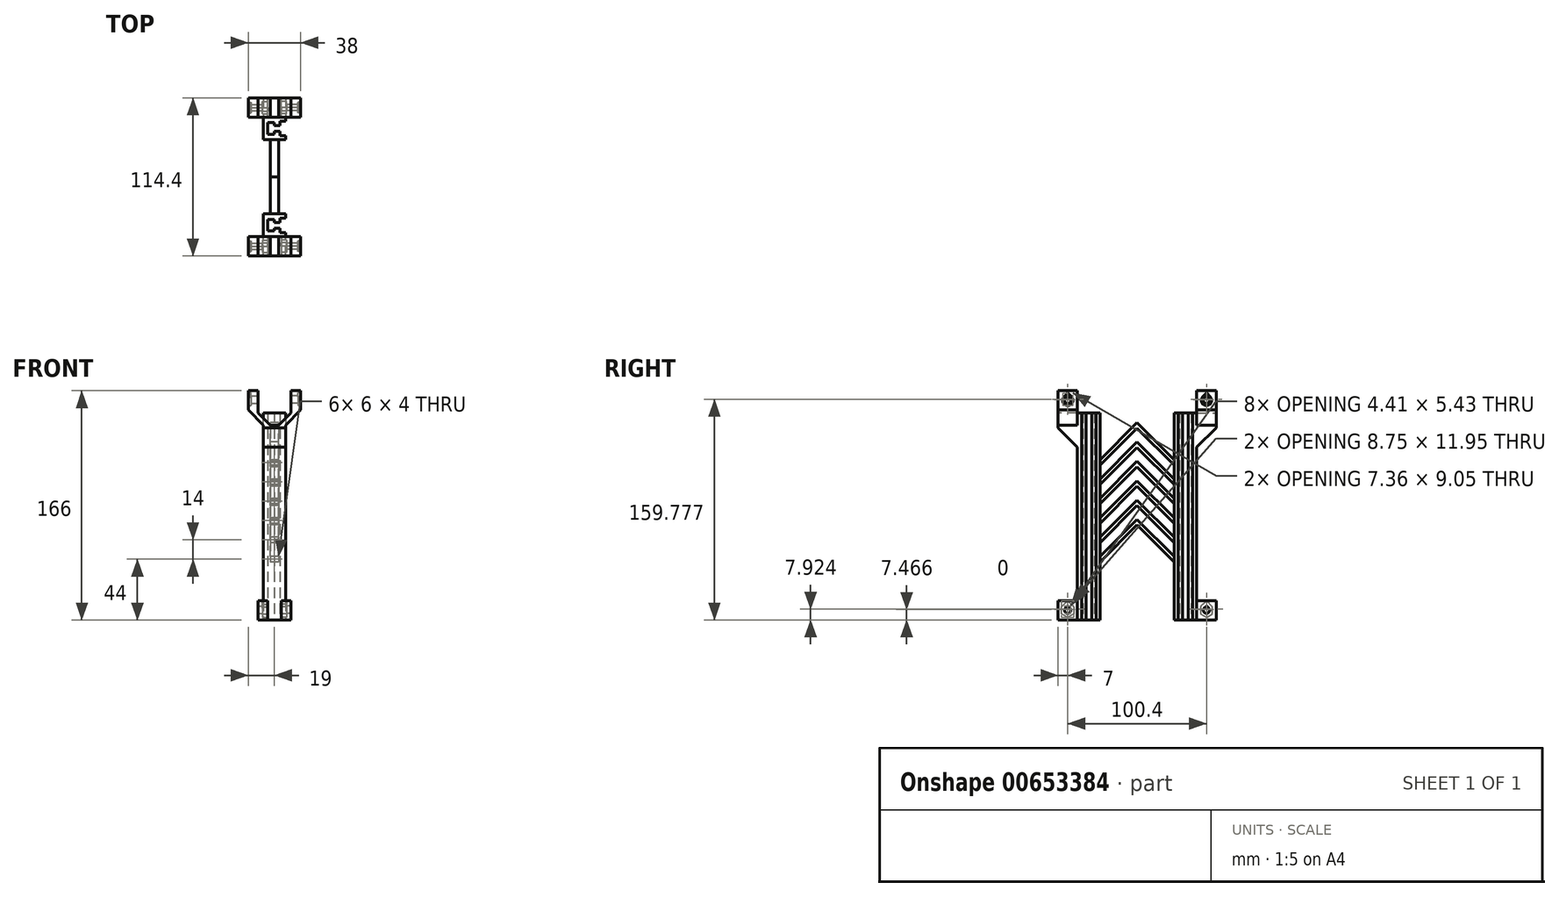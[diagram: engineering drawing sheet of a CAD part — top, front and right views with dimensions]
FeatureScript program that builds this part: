
annotation { "Feature Type Name" : "Feature", "Feature Type Description" : "" }
export const myFeature = defineFeature(function(context is Context, id is Id, definition is map)
    precondition{}
    {
        {
            var Q0;
            Q0=qCreatedBy(makeId("Top.planeOp"),FACE);
            var sketch = newSketch(context, id + "F0", { "sketchPlane" : qUnion([Q0])});
            skLineSegment(sketch, "E0", {"start": v(0, 0) * mm, "end": v(5, 0) * mm});
            skLineSegment(sketch, "E1", {"start": v(5, 0) * mm, "end": v(5, -2.1) * mm});
            skLineSegment(sketch, "E2", {"start": v(5, -2.1) * mm, "end": v(9, -2.1) * mm});
            skLineSegment(sketch, "E3", {"start": v(9, -2.1) * mm, "end": v(9, 1) * mm});
            skLineSegment(sketch, "E4", {"start": v(9, 1) * mm, "end": v(13, 1) * mm});
            skLineSegment(sketch, "E5", {"start": v(13, 1) * mm, "end": v(13, 4) * mm});
            skLineSegment(sketch, "E6", {"start": v(13, 4) * mm, "end": v(-3, 4) * mm});
            skLineSegment(sketch, "E7", {"start": v(-3, 4) * mm, "end": v(-3, -12.4) * mm});
            skLineSegment(sketch, "E8", {"start": v(-3, -12.4) * mm, "end": v(13, -12.4) * mm});
            skLineSegment(sketch, "E9", {"start": v(13, -12.4) * mm, "end": v(13, -9.4) * mm});
            skLineSegment(sketch, "E10", {"start": v(13, -9.4) * mm, "end": v(9, -9.4) * mm});
            skLineSegment(sketch, "E11", {"start": v(9, -9.4) * mm, "end": v(9, -6.3) * mm});
            skLineSegment(sketch, "E12", {"start": v(9, -6.3) * mm, "end": v(5, -6.3) * mm});
            skLineSegment(sketch, "E13", {"start": v(5, -6.3) * mm, "end": v(5, -8.4) * mm});
            skLineSegment(sketch, "E14", {"start": v(5, -8.4) * mm, "end": v(0, -8.4) * mm});
            skLineSegment(sketch, "E15", {"start": v(0, -8.4) * mm, "end": v(0, 0) * mm});
            skLineSegment(sketch, "E16", {"start": v(0, 0) * mm, "end": v(-3, 0) * mm});
            skLineSegment(sketch, "E17", {"start": v(0, -8.4) * mm, "end": v(-3, -8.4) * mm});
            skLineSegment(sketch, "E18", {"start": v(13, -9.4) * mm, "end": v(13, 1) * mm});
            skLineSegment(sketch, "E19", {"start": v(13, -12.4) * mm, "end": v(9.8, -12.4) * mm});
            skLineSegment(sketch, "E20", {"start": v(13, -12.4) * mm, "end": v(5, -12.4) * mm});
            skSolve(sketch);
        }
        {
            var Q0;
            Q0=makeQuery(id+"F0.imprint","IMPRINT",FACE,{"disambiguationData":[TD([[makeQuery(id+"F0.imprint","IMPRINT",EDGE,{"derivedFrom":sQuery(id+"F0.wireOp",EDGE,"E0")}),1.0]])]});
            var Q1;
            {var subQ0=sQuery(id+"F0.wireOp",EDGE,"E8");Q1=makeQuery(id+"F0.imprint","IMPRINT",FACE,{"disambiguationData":[TD([[makeQuery(id+"F0.imprint","IMPRINT",EDGE,{"derivedFrom":subQ0}),1.0]])]});}
            var Q2;
            Q2=makeQuery(id+"F0.imprint","IMPRINT",FACE,{"disambiguationData":[TD([[makeQuery(id+"F0.imprint","IMPRINT",EDGE,{"derivedFrom":sQuery(id+"F0.wireOp",EDGE,"E15")}),1.0]])]});
            extrude(context, id + "F1", {"entities" : qUnion([Q0, Q1, Q2]), "depth" : 150 * mm, "offsetDistance" : 25 * mm});
        }
        {
            var Q0;
            Q0=sQuery(id+"F0.wireOp",EDGE,"E8");
            var Q1;
            Q1=sQuery(id+"F0.wireOp",VERTEX,"E19.end");
            cPlane(context, id + "F2", {"entities" : qUnion([Q0, Q1]), "cplaneType" : CPlaneType.LINE_POINT, "offset" : 25 * mm, "width" : 150 * mm, "height" : 150 * mm});
        }
        {
            var Q0;
            Q0=qCreatedBy(id+"F2.planeOp",FACE);
            var sketch = newSketch(context, id + "F3", { "sketchPlane" : qUnion([Q0])});
            skPoint(sketch, "E21.0", {"position": v(-12.4, 0) * mm});
            skLineSegment(sketch, "E22.bottom", {"start": v(-12.4, 0) * mm, "end": v(-26.4, 0) * mm});
            skLineSegment(sketch, "E22.top", {"start": v(-12.4, 14) * mm, "end": v(-26.4, 14) * mm});
            skLineSegment(sketch, "E22.left", {"start": v(-12.4, 0) * mm, "end": v(-12.4, 14) * mm});
            skLineSegment(sketch, "E22.right", {"start": v(-26.4, 0) * mm, "end": v(-26.4, 14) * mm});
            skLineSegment(sketch, "E23", {"start": v(-19.4, 0) * mm, "end": v(-19.4, 7) * mm});
            skCircle(sketch, "E24", {"center": v(-19.4, 7) * mm, "radius": 5.05 * mm});
            skCircle(sketch, "E25.cCircle", {"center": v(-19.4, 7) * mm, "radius": 5.05 * mm, "construction": true});
            skLineSegment(sketch, "E25.0", {"start": v(-19.4, 12.05) * mm, "end": v(-15.03, 9.53) * mm});
            skLineSegment(sketch, "E25.1", {"start": v(-15.03, 9.53) * mm, "end": v(-15.03, 4.48) * mm});
            skLineSegment(sketch, "E25.2", {"start": v(-15.03, 4.48) * mm, "end": v(-19.4, 1.95) * mm});
            skLineSegment(sketch, "E25.3", {"start": v(-19.4, 1.95) * mm, "end": v(-23.77, 4.47) * mm});
            skLineSegment(sketch, "E25.4", {"start": v(-23.77, 4.47) * mm, "end": v(-23.77, 9.52) * mm});
            skLineSegment(sketch, "E25.5", {"start": v(-23.77, 9.52) * mm, "end": v(-19.4, 12.05) * mm});
            skLineSegment(sketch, "E26", {"start": v(-19.4, 7) * mm, "end": v(-24.45, 7) * mm});
            skLineSegment(sketch, "E27", {"start": v(-24.45, 7) * mm, "end": v(-19.4, 12.05) * mm});
            skLineSegment(sketch, "E28", {"start": v(-23.77, 9.52) * mm, "end": v(-19.4, 13.9) * mm});
            skLineSegment(sketch, "E29", {"start": v(-19.4, 13.9) * mm, "end": v(-15.03, 9.53) * mm});
            skLineSegment(sketch, "E30", {"start": v(-15.03, 9.53) * mm, "end": v(-16.88, 11.37) * mm});
            skSolve(sketch);
        }
        {
            var Q0;
            Q0=makeQuery(id+"F3.imprint","IMPRINT",FACE,{"disambiguationData":[TD([[makeQuery(id+"F3.imprint","IMPRINT",EDGE,{"derivedFrom":sQuery(id+"F3.wireOp",EDGE,"E22.top")}),1.0]])]});
            var Q1;
            {var subQ0=sQuery(id+"F3.wireOp",EDGE,"E25.1");Q1=makeQuery(id+"F3.imprint","IMPRINT",FACE,{"disambiguationData":[TD([[makeQuery(id+"F3.imprint","IMPRINT",EDGE,{"derivedFrom":subQ0}),1.0]])]});}
            var Q2;
            {var subQ0=sQuery(id+"F3.wireOp",EDGE,"E25.2");Q2=makeQuery(id+"F3.imprint","IMPRINT",FACE,{"disambiguationData":[TD([[makeQuery(id+"F3.imprint","IMPRINT",EDGE,{"derivedFrom":subQ0}),1.0]])]});}
            var Q3;
            {var subQ0=sQuery(id+"F3.wireOp",EDGE,"E25.3");Q3=makeQuery(id+"F3.imprint","IMPRINT",FACE,{"disambiguationData":[TD([[makeQuery(id+"F3.imprint","IMPRINT",EDGE,{"derivedFrom":subQ0}),1.0]])]});}
            var Q4;
            {var subQ0=sQuery(id+"F3.wireOp",EDGE,"E25.4");Q4=makeQuery(id+"F3.imprint","IMPRINT",FACE,{"disambiguationData":[TD([[makeQuery(id+"F3.imprint","IMPRINT",EDGE,{"derivedFrom":subQ0}),1.0]])]});}
            var Q5;
            {var subQ0=sQuery(id+"F3.wireOp",EDGE,"E28");var subQ1=sQuery(id+"F3.wireOp",EDGE,"E24");var subQ3=makeQuery(id+"F3.imprint","INTERSECT",VERTEX,{"derivedFrom":[subQ1,subQ0]});Q5=makeQuery(id+"F3.imprint","IMPRINT",FACE,{"disambiguationData":[TD([[makeQuery(id+"F3.imprint","IMPRINT",EDGE,{"disambiguationData":[TD([[subQ3,-1.0]])],"derivedFrom":subQ1}),1.0]])]});}
            var Q6;
            {var subQ0=sQuery(id+"F3.wireOp",EDGE,"E30");Q6=makeQuery(id+"F3.imprint","IMPRINT",FACE,{"disambiguationData":[TD([[makeQuery(id+"F3.imprint","IMPRINT",EDGE,{"derivedFrom":subQ0}),-1.0]])]});}
            extrude(context, id + "F4", {"entities" : qUnion([Q0, Q1, Q2, Q3, Q4, Q5, Q6]), "depth" : 4 * mm, "offsetDistance" : 25 * mm});
        }
        {
            var Q0;
            Q0=makeQuery(id+"F4.opExtrude","CAP_FACE",FACE,{"disambiguationData":[OSD([sQuery(id+"F3.wireOp",EDGE,"E22.bottom"),sQuery(id+"F3.wireOp",EDGE,"E22.top"),sQuery(id+"F3.wireOp",EDGE,"E22.left"),sQuery(id+"F3.wireOp",EDGE,"E22.right"),sQuery(id+"F3.wireOp",EDGE,"E25.0"),sQuery(id+"F3.wireOp",EDGE,"E25.1"),sQuery(id+"F3.wireOp",EDGE,"E25.2"),sQuery(id+"F3.wireOp",EDGE,"E25.3"),sQuery(id+"F3.wireOp",EDGE,"E25.4"),sQuery(id+"F3.wireOp",EDGE,"E25.5")])],"isStart":false});
            var sketch = newSketch(context, id + "F5", { "sketchPlane" : qUnion([Q0])});
            skPoint(sketch, "E31.0", {"position": v(-19.4, 7) * mm});
            skLineSegment(sketch, "E32.bottom", {"start": v(-12.4, 0) * mm, "end": v(-26.4, 0) * mm});
            skLineSegment(sketch, "E32.top", {"start": v(-12.4, 14) * mm, "end": v(-26.4, 14) * mm});
            skLineSegment(sketch, "E32.left", {"start": v(-12.4, 0) * mm, "end": v(-12.4, 14) * mm});
            skLineSegment(sketch, "E32.right", {"start": v(-26.4, 0) * mm, "end": v(-26.4, 14) * mm});
            skCircle(sketch, "E33", {"center": v(-19.4, 7) * mm, "radius": 2.25 * mm});
            skLineSegment(sketch, "E34", {"start": v(-17.15, 7) * mm, "end": v(-19.4, 9.25) * mm});
            skLineSegment(sketch, "E35", {"start": v(-19.4, 7) * mm, "end": v(-17.8, 8.6) * mm});
            skLineSegment(sketch, "E36", {"start": v(-17.8, 8.6) * mm, "end": v(-19.4, 10.18) * mm});
            skLineSegment(sketch, "E37", {"start": v(-19.4, 10.18) * mm, "end": v(-21, 8.6) * mm});
            skSolve(sketch);
        }
        {
            var Q0;
            Q0=makeQuery(id+"F5.imprint","IMPRINT",FACE,{"disambiguationData":[TD([[makeQuery(id+"F5.imprint","IMPRINT",EDGE,{"derivedFrom":sQuery(id+"F5.wireOp",EDGE,"E32.bottom")}),-1.0]])]});
            var Q1;
            {var subQ0=sQuery(id+"F5.wireOp",EDGE,"E36");Q1=makeQuery(id+"F5.imprint","IMPRINT",FACE,{"disambiguationData":[TD([[makeQuery(id+"F5.imprint","IMPRINT",EDGE,{"derivedFrom":subQ0}),-1.0]])]});}
            extrude(context, id + "F6", {"entities" : qUnion([Q0, Q1]), "operationType" : NewBodyOperationType.ADD, "depth" : 3 * mm, "offsetDistance" : 25 * mm});
        }
        {
            var Q0;
            Q0=sQuery(id+"F0.wireOp",EDGE,"E8");
            var Q1;
            Q1=sQuery(id+"F0.wireOp",VERTEX,"E20.end");
            cPlane(context, id + "F7", {"entities" : qUnion([Q0, Q1]), "cplaneType" : CPlaneType.LINE_POINT, "offset" : 25 * mm, "width" : 150 * mm, "height" : 150 * mm});
        }
        {
            var Q0;
            Q0=makeQuery(id+"F4.opExtrude","SWEPT_BODY",BODY,{"disambiguationData":[OSD([sQuery(id+"F3.wireOp",EDGE,"E22.bottom"),sQuery(id+"F3.wireOp",EDGE,"E22.top"),sQuery(id+"F3.wireOp",EDGE,"E22.left"),sQuery(id+"F3.wireOp",EDGE,"E22.right"),sQuery(id+"F3.wireOp",EDGE,"E25.0"),sQuery(id+"F3.wireOp",EDGE,"E25.1"),sQuery(id+"F3.wireOp",EDGE,"E25.2"),sQuery(id+"F3.wireOp",EDGE,"E25.3"),sQuery(id+"F3.wireOp",EDGE,"E25.4"),sQuery(id+"F3.wireOp",EDGE,"E25.5")])]});
            var Q1;
            Q1=makeQuery(id+"F6.opExtrude","SWEPT_BODY",BODY,{"disambiguationData":[OSD([sQuery(id+"F5.wireOp",EDGE,"E32.bottom"),sQuery(id+"F5.wireOp",EDGE,"E32.top"),sQuery(id+"F5.wireOp",EDGE,"E32.left"),sQuery(id+"F5.wireOp",EDGE,"E32.right"),sQuery(id+"F5.wireOp",EDGE,"E33")])]});
            var Q2;
            Q2=qCreatedBy(id+"F7.planeOp",FACE);
            mirror(context, id + "F8", {"operationType" : NewBodyOperationType.ADD, "entities" : qUnion([Q0, Q1]), "mirrorPlane" : qUnion([Q2])});
        }
        {
            var Q0;
            Q0=makeQuery(id+"F1.opExtrude","SWEPT_FACE",FACE,{"disambiguationData":[OSD([sQuery(id+"F0.wireOp",EDGE,"E7")])]});
            var sketch = newSketch(context, id + "F9", { "sketchPlane" : qUnion([Q0])});
            skPoint(sketch, "E38.0", {"position": v(12.4, 150) * mm});
            skLineSegment(sketch, "E39", {"start": v(12.4, 150) * mm, "end": v(12.4, 125) * mm});
            skLineSegment(sketch, "E40", {"start": v(12.4, 125) * mm, "end": v(26.4, 125) * mm});
            skLineSegment(sketch, "E41", {"start": v(26.4, 125) * mm, "end": v(26.4, 139) * mm});
            skLineSegment(sketch, "E42", {"start": v(26.4, 139) * mm, "end": v(12.4, 125) * mm});
            skLineSegment(sketch, "E43", {"start": v(26.4, 139) * mm, "end": v(26.4, 141) * mm});
            skLineSegment(sketch, "E44", {"start": v(26.4, 141) * mm, "end": v(12.4, 141) * mm});
            skSolve(sketch);
        }
        {
            var Q0;
            {var subQ0=sQuery(id+"F9.wireOp",EDGE,"E42");Q0=makeQuery(id+"F9.imprint","IMPRINT",FACE,{"disambiguationData":[TD([[makeQuery(id+"F9.imprint","IMPRINT",EDGE,{"derivedFrom":subQ0}),-1.0]])]});}
            extrude(context, id + "F10", {"entities" : qUnion([Q0]), "oppositeDirection" : true, "depth" : 16 * mm, "offsetDistance" : 25 * mm});
        }
        {
            var Q0;
            Q0=makeQuery(id+"F10.opExtrude","SWEPT_FACE",FACE,{"disambiguationData":[OSD([sQuery(id+"F9.wireOp",EDGE,"E43")])]});
            var sketch = newSketch(context, id + "F11", { "sketchPlane" : qUnion([Q0])});
            skPoint(sketch, "E45.0", {"position": v(13, 141) * mm});
            skPoint(sketch, "E46.0", {"position": v(-3, 141) * mm});
            skLineSegment(sketch, "E47", {"start": v(13, 141) * mm, "end": v(24, 141) * mm});
            skLineSegment(sketch, "E48", {"start": v(24, 141) * mm, "end": v(24, 152) * mm});
            skLineSegment(sketch, "E49", {"start": v(24, 152) * mm, "end": v(13, 141) * mm});
            skLineSegment(sketch, "E50", {"start": v(24, 152) * mm, "end": v(17, 152) * mm});
            skLineSegment(sketch, "E51", {"start": v(17, 152) * mm, "end": v(17, 150) * mm});
            skLineSegment(sketch, "E52", {"start": v(17, 150) * mm, "end": v(8, 141) * mm});
            skLineSegment(sketch, "E53", {"start": v(5, 141) * mm, "end": v(5, 151) * mm});
            skLineSegment(sketch, "E54.MirrorCS", {"start": v(-7, 150) * mm, "end": v(2, 141) * mm});
            skLineSegment(sketch, "E55.MirrorCS", {"start": v(-7, 152) * mm, "end": v(-7, 150) * mm});
            skLineSegment(sketch, "E56.MirrorCS", {"start": v(-14, 152) * mm, "end": v(-7, 152) * mm});
            skLineSegment(sketch, "E57.MirrorCS", {"start": v(-3, 141) * mm, "end": v(-14, 141) * mm});
            skLineSegment(sketch, "E58.MirrorCS", {"start": v(-14, 152) * mm, "end": v(-3, 141) * mm});
            skLineSegment(sketch, "E59.MirrorCS", {"start": v(-14, 141) * mm, "end": v(-14, 152) * mm});
            skSolve(sketch);
        }
        {
            var Q0;
            {var subQ1=sQuery(id+"F11.wireOp",EDGE,"E49");Q0=makeQuery(id+"F11.imprint","IMPRINT",FACE,{"disambiguationData":[TD([[makeQuery(id+"F11.imprint","IMPRINT",EDGE,{"derivedFrom":subQ1}),-1.0]])]});}
            var Q1;
            {var subQ1=sQuery(id+"F11.wireOp",EDGE,"E54.MirrorCS");Q1=makeQuery(id+"F11.imprint","IMPRINT",FACE,{"disambiguationData":[TD([[makeQuery(id+"F11.imprint","IMPRINT",EDGE,{"derivedFrom":subQ1}),-1.0]])]});}
            extrude(context, id + "F12", {"entities" : qUnion([Q0, Q1]), "oppositeDirection" : true, "depth" : 14 * mm, "offsetDistance" : 25 * mm});
        }
        {
            var Q0;
            Q0=makeQuery(id+"F12.opExtrude","SWEPT_FACE",FACE,{"disambiguationData":[OSD([sQuery(id+"F11.wireOp",EDGE,"E55.MirrorCS")])]});
            var sketch = newSketch(context, id + "F13", { "sketchPlane" : qUnion([Q0])});
            skPoint(sketch, "E60.0", {"position": v(-19.4, 152) * mm});
            skLineSegment(sketch, "E61", {"start": v(-19.4, 152) * mm, "end": v(-19.4, 159) * mm});
            skLineSegment(sketch, "E62.bottom", {"start": v(-12.4, 152) * mm, "end": v(-26.4, 152) * mm});
            skLineSegment(sketch, "E62.top", {"start": v(-12.4, 166) * mm, "end": v(-26.4, 166) * mm});
            skLineSegment(sketch, "E62.left", {"start": v(-12.4, 152) * mm, "end": v(-12.4, 166) * mm});
            skLineSegment(sketch, "E62.right", {"start": v(-26.4, 152) * mm, "end": v(-26.4, 166) * mm});
            skPoint(sketch, "E62.middle", {"position": v(-19.4, 159) * mm});
            skCircle(sketch, "E63", {"center": v(-19.4, 159) * mm, "radius": 2.25 * mm});
            skLineSegment(sketch, "E64", {"start": v(-17.15, 159) * mm, "end": v(-19.4, 161.25) * mm});
            skLineSegment(sketch, "E65", {"start": v(-19.4, 159) * mm, "end": v(-17.8, 160.6) * mm});
            skLineSegment(sketch, "E66", {"start": v(-17.8, 160.6) * mm, "end": v(-19.4, 162.18) * mm});
            skLineSegment(sketch, "E67", {"start": v(-19.4, 162.18) * mm, "end": v(-21, 160.6) * mm});
            skSolve(sketch);
        }
        {
            var Q0;
            Q0=makeQuery(id+"F13.imprint","IMPRINT",FACE,{"disambiguationData":[TD([[makeQuery(id+"F13.imprint","IMPRINT",EDGE,{"derivedFrom":sQuery(id+"F13.wireOp",EDGE,"E62.top")}),1.0]])]});
            extrude(context, id + "F14", {"entities" : qUnion([Q0]), "oppositeDirection" : true, "depth" : 5 * mm, "offsetDistance" : 25 * mm});
        }
        {
            var Q0;
            Q0=makeQuery(id+"F14.opExtrude","CAP_FACE",FACE,{"disambiguationData":[OSD([sQuery(id+"F13.wireOp",EDGE,"E62.bottom"),sQuery(id+"F13.wireOp",EDGE,"E62.top"),sQuery(id+"F13.wireOp",EDGE,"E62.left"),sQuery(id+"F13.wireOp",EDGE,"E62.right"),sQuery(id+"F13.wireOp",EDGE,"E63")])],"isStart":false});
            var sketch = newSketch(context, id + "F15", { "sketchPlane" : qUnion([Q0])});
            skPoint(sketch, "E68.0", {"position": v(19.4, 159) * mm});
            skLineSegment(sketch, "E69.bottom", {"start": v(26.4, 166) * mm, "end": v(12.4, 166) * mm});
            skLineSegment(sketch, "E69.top", {"start": v(26.4, 152) * mm, "end": v(12.4, 152) * mm});
            skLineSegment(sketch, "E69.left", {"start": v(26.4, 166) * mm, "end": v(26.4, 152) * mm});
            skLineSegment(sketch, "E69.right", {"start": v(12.4, 166) * mm, "end": v(12.4, 152) * mm});
            skCircle(sketch, "E70", {"center": v(19.4, 159) * mm, "radius": 3.75 * mm});
            skLineSegment(sketch, "E71", {"start": v(23.15, 159) * mm, "end": v(19.4, 162.75) * mm});
            skLineSegment(sketch, "E72", {"start": v(19.4, 159) * mm, "end": v(22.05, 161.65) * mm});
            skLineSegment(sketch, "E73", {"start": v(22.05, 161.65) * mm, "end": v(19.4, 164.3) * mm});
            skLineSegment(sketch, "E74", {"start": v(19.4, 164.3) * mm, "end": v(16.75, 161.65) * mm});
            skSolve(sketch);
        }
        {
            var Q0;
            Q0=makeQuery(id+"F15.imprint","IMPRINT",FACE,{"disambiguationData":[TD([[makeQuery(id+"F15.imprint","IMPRINT",EDGE,{"derivedFrom":sQuery(id+"F15.wireOp",EDGE,"E69.bottom")}),-1.0]])]});
            extrude(context, id + "F16", {"entities" : qUnion([Q0]), "depth" : 2 * mm, "offsetDistance" : 25 * mm});
        }
        {
            var Q0;
            Q0=makeQuery(id+"F14.opExtrude","SWEPT_BODY",BODY,{"disambiguationData":[OSD([sQuery(id+"F13.wireOp",EDGE,"E62.bottom"),sQuery(id+"F13.wireOp",EDGE,"E62.top"),sQuery(id+"F13.wireOp",EDGE,"E62.left"),sQuery(id+"F13.wireOp",EDGE,"E62.right"),sQuery(id+"F13.wireOp",EDGE,"E63")])]});
            var Q1;
            Q1=makeQuery(id+"F16.opExtrude","SWEPT_BODY",BODY,{"disambiguationData":[OSD([sQuery(id+"F15.wireOp",EDGE,"E69.bottom"),sQuery(id+"F15.wireOp",EDGE,"E69.top"),sQuery(id+"F15.wireOp",EDGE,"E69.left"),sQuery(id+"F15.wireOp",EDGE,"E69.right"),sQuery(id+"F15.wireOp",EDGE,"E70")])]});
            var Q2;
            Q2=qCreatedBy(id+"F7.planeOp",FACE);
            mirror(context, id + "F17", {"operationType" : NewBodyOperationType.ADD, "entities" : qUnion([Q0, Q1]), "mirrorPlane" : qUnion([Q2])});
        }
        {
            var Q0;
            Q0=makeQuery(id+"F1.opExtrude","SWEPT_FACE",FACE,{"disambiguationData":[OSD([sQuery(id+"F0.wireOp",EDGE,"E7")])]});
            var sketch = newSketch(context, id + "F18", { "sketchPlane" : qUnion([Q0])});
            skPoint(sketch, "E75.0", {"position": v(-4, 0) * mm});
            skLineSegment(sketch, "E76", {"start": v(-4, 0) * mm, "end": v(-30.8, 0) * mm});
            skLineSegment(sketch, "E77", {"start": v(-30.8, 0) * mm, "end": v(-30.8, 26.8) * mm});
            skLineSegment(sketch, "E78", {"start": v(-30.8, 26.8) * mm, "end": v(-4, 0) * mm});
            skLineSegment(sketch, "E79", {"start": v(-4, 0) * mm, "end": v(-4, 4) * mm});
            skLineSegment(sketch, "E80", {"start": v(-4, 4) * mm, "end": v(-30.8, 30.8) * mm});
            skLineSegment(sketch, "E81", {"start": v(-30.8, 30.8) * mm, "end": v(-30.8, 26.8) * mm});
            skSolve(sketch);
        }
        {
            var Q0;
            Q0=makeQuery(id+"F18.imprint","IMPRINT",FACE,{"disambiguationData":[TD([[makeQuery(id+"F18.imprint","IMPRINT",EDGE,{"derivedFrom":sQuery(id+"F18.wireOp",EDGE,"E78")}),1.0]])]});
            extrude(context, id + "F19", {"entities" : qUnion([Q0]), "oppositeDirection" : true, "depth" : 11 * mm, "offsetDistance" : 25 * mm});
        }
        {
            var Q0;
            Q0=makeQuery(id+"F19.opExtrude","CAP_FACE",FACE,{"disambiguationData":[OSD([sQuery(id+"F18.wireOp",EDGE,"E78"),sQuery(id+"F18.wireOp",EDGE,"E79"),sQuery(id+"F18.wireOp",EDGE,"E80"),sQuery(id+"F18.wireOp",EDGE,"E81")])],"isStart":true});
            extrude(context, id + "F20", {"entities" : qUnion([Q0]), "operationType" : NewBodyOperationType.REMOVE, "oppositeDirection" : true, "depth" : 5 * mm, "offsetDistance" : 25 * mm});
        }
        {
            var Q0;
            Q0=makeQuery(id+"F19.opExtrude","SWEPT_BODY",BODY,{"disambiguationData":[OSD([sQuery(id+"F18.wireOp",EDGE,"E78"),sQuery(id+"F18.wireOp",EDGE,"E79"),sQuery(id+"F18.wireOp",EDGE,"E80"),sQuery(id+"F18.wireOp",EDGE,"E81")])]});
            transform(context, id + "F21", {"entities" : qUnion([Q0]), "transformType" : TransformType.TRANSLATION_3D, "dx" : 0 * mm, "dy" : 0 * mm, "dz" : 28 * mm, "makeCopy" : true});
        }
        {
            var Q0;
            Q0=makeQuery(id+"F21.opPattern","COPY",BODY,{"derivedFrom":makeQuery(id+"F19.opExtrude","SWEPT_BODY",BODY,{"disambiguationData":[OSD([sQuery(id+"F18.wireOp",EDGE,"E78"),sQuery(id+"F18.wireOp",EDGE,"E79"),sQuery(id+"F18.wireOp",EDGE,"E80"),sQuery(id+"F18.wireOp",EDGE,"E81")])]}),"instanceName":"1"});
            transform(context, id + "F22", {"entities" : qUnion([Q0]), "transformType" : TransformType.TRANSLATION_3D, "dx" : 0 * mm, "dy" : 0 * mm, "dz" : 28 * mm, "makeCopy" : true});
        }
        {
            var Q0;
            Q0=makeQuery(id+"F22.opPattern","COPY",BODY,{"derivedFrom":makeQuery(id+"F21.opPattern","COPY",BODY,{"derivedFrom":makeQuery(id+"F19.opExtrude","SWEPT_BODY",BODY,{"disambiguationData":[OSD([sQuery(id+"F18.wireOp",EDGE,"E78"),sQuery(id+"F18.wireOp",EDGE,"E79"),sQuery(id+"F18.wireOp",EDGE,"E80"),sQuery(id+"F18.wireOp",EDGE,"E81")])]}),"instanceName":"1"}),"instanceName":"1"});
            transform(context, id + "F23", {"entities" : qUnion([Q0]), "transformType" : TransformType.TRANSLATION_3D, "dx" : 0 * mm, "dy" : 0 * mm, "dz" : 28 * mm, "makeCopy" : true});
        }
        {
            var Q0;
            Q0=makeQuery(id+"F23.opPattern","COPY",BODY,{"derivedFrom":makeQuery(id+"F22.opPattern","COPY",BODY,{"derivedFrom":makeQuery(id+"F21.opPattern","COPY",BODY,{"derivedFrom":makeQuery(id+"F19.opExtrude","SWEPT_BODY",BODY,{"disambiguationData":[OSD([sQuery(id+"F18.wireOp",EDGE,"E78"),sQuery(id+"F18.wireOp",EDGE,"E79"),sQuery(id+"F18.wireOp",EDGE,"E80"),sQuery(id+"F18.wireOp",EDGE,"E81")])]}),"instanceName":"1"}),"instanceName":"1"}),"instanceName":"1"});
            transform(context, id + "F24", {"entities" : qUnion([Q0]), "transformType" : TransformType.TRANSLATION_3D, "dx" : 0 * mm, "dy" : 0 * mm, "dz" : 28 * mm, "makeCopy" : true});
        }
        {
            var Q0;
            Q0=makeQuery(id+"F24.opPattern","COPY",FACE,{"derivedFrom":makeQuery(id+"F23.opPattern","COPY",FACE,{"derivedFrom":makeQuery(id+"F22.opPattern","COPY",FACE,{"derivedFrom":makeQuery(id+"F21.opPattern","COPY",FACE,{"derivedFrom":makeQuery(id+"F19.opExtrude","SWEPT_FACE",FACE,{"disambiguationData":[OSD([sQuery(id+"F18.wireOp",EDGE,"E81")])]}),"instanceName":"1"}),"instanceName":"1"}),"instanceName":"1"}),"instanceName":"1"});
            cPlane(context, id + "F25", {"entities" : qUnion([Q0]), "cplaneType" : CPlaneType.OFFSET, "offset" : 0 * mm, "width" : 150 * mm, "height" : 150 * mm});
        }
        {
            var Q0;
            Q0=makeQuery(id+"F21.opPattern","COPY",BODY,{"derivedFrom":makeQuery(id+"F19.opExtrude","SWEPT_BODY",BODY,{"disambiguationData":[OSD([sQuery(id+"F18.wireOp",EDGE,"E78"),sQuery(id+"F18.wireOp",EDGE,"E79"),sQuery(id+"F18.wireOp",EDGE,"E80"),sQuery(id+"F18.wireOp",EDGE,"E81")])]}),"instanceName":"1"});
            transform(context, id + "F26", {"entities" : qUnion([Q0]), "transformType" : TransformType.TRANSLATION_3D, "dx" : 0 * mm, "dy" : 0 * mm, "dz" : 14 * mm, "makeCopy" : false});
        }
        {
            var Q0;
            Q0=makeQuery(id+"F22.opPattern","COPY",BODY,{"derivedFrom":makeQuery(id+"F21.opPattern","COPY",BODY,{"derivedFrom":makeQuery(id+"F19.opExtrude","SWEPT_BODY",BODY,{"disambiguationData":[OSD([sQuery(id+"F18.wireOp",EDGE,"E78"),sQuery(id+"F18.wireOp",EDGE,"E79"),sQuery(id+"F18.wireOp",EDGE,"E80"),sQuery(id+"F18.wireOp",EDGE,"E81")])]}),"instanceName":"1"}),"instanceName":"1"});
            var Q1;
            Q1=makeQuery(id+"F23.opPattern","COPY",BODY,{"derivedFrom":makeQuery(id+"F22.opPattern","COPY",BODY,{"derivedFrom":makeQuery(id+"F21.opPattern","COPY",BODY,{"derivedFrom":makeQuery(id+"F19.opExtrude","SWEPT_BODY",BODY,{"disambiguationData":[OSD([sQuery(id+"F18.wireOp",EDGE,"E78"),sQuery(id+"F18.wireOp",EDGE,"E79"),sQuery(id+"F18.wireOp",EDGE,"E80"),sQuery(id+"F18.wireOp",EDGE,"E81")])]}),"instanceName":"1"}),"instanceName":"1"}),"instanceName":"1"});
            transform(context, id + "F27", {"entities" : qUnion([Q0, Q1]), "transformType" : TransformType.TRANSLATION_3D, "dx" : 0 * mm, "dy" : 0 * mm, "dz" : 14 * mm, "makeCopy" : true});
        }
        {
            var Q0;
            Q0=makeQuery(id+"F19.opExtrude","SWEPT_BODY",BODY,{"disambiguationData":[OSD([sQuery(id+"F18.wireOp",EDGE,"E78"),sQuery(id+"F18.wireOp",EDGE,"E79"),sQuery(id+"F18.wireOp",EDGE,"E80"),sQuery(id+"F18.wireOp",EDGE,"E81")])]});
            deleteBodies(context, id + "F28", {"entities" : qUnion([Q0])});
        }
        {
            var Q0;
            Q0=makeQuery(id+"F1.opExtrude","SWEPT_BODY",BODY,{"disambiguationData":[OSD([sQuery(id+"F0.wireOp",EDGE,"E0"),sQuery(id+"F0.wireOp",EDGE,"E1"),sQuery(id+"F0.wireOp",EDGE,"E2"),sQuery(id+"F0.wireOp",EDGE,"E3"),sQuery(id+"F0.wireOp",EDGE,"E4"),sQuery(id+"F0.wireOp",EDGE,"E5"),sQuery(id+"F0.wireOp",EDGE,"E6"),sQuery(id+"F0.wireOp",EDGE,"E7"),sQuery(id+"F0.wireOp",EDGE,"E8"),sQuery(id+"F0.wireOp",EDGE,"E9"),sQuery(id+"F0.wireOp",EDGE,"E10"),sQuery(id+"F0.wireOp",EDGE,"E11"),sQuery(id+"F0.wireOp",EDGE,"E12"),sQuery(id+"F0.wireOp",EDGE,"E13"),sQuery(id+"F0.wireOp",EDGE,"E14"),sQuery(id+"F0.wireOp",EDGE,"E15"),sQuery(id+"F0.wireOp",EDGE,"E20")])]});
            var Q1;
            Q1=makeQuery(id+"F10.opExtrude","SWEPT_BODY",BODY,{"disambiguationData":[OSD([sQuery(id+"F9.wireOp",EDGE,"E39"),sQuery(id+"F9.wireOp",EDGE,"E42"),sQuery(id+"F9.wireOp",EDGE,"E43"),sQuery(id+"F9.wireOp",EDGE,"E44")])]});
            var Q2;
            Q2=makeQuery(id+"F12.opExtrude","SWEPT_BODY",BODY,{"disambiguationData":[OSD([sQuery(id+"F9.wireOp",EDGE,"E43"),sQuery(id+"F9.wireOp",EDGE,"E44"),sQuery(id+"F11.wireOp",EDGE,"E49"),sQuery(id+"F11.wireOp",EDGE,"E50"),sQuery(id+"F11.wireOp",EDGE,"E51"),sQuery(id+"F11.wireOp",EDGE,"E52")])]});
            var Q3;
            Q3=makeQuery(id+"F12.opExtrude","SWEPT_BODY",BODY,{"disambiguationData":[OSD([sQuery(id+"F9.wireOp",EDGE,"E43"),sQuery(id+"F9.wireOp",EDGE,"E44"),sQuery(id+"F11.wireOp",EDGE,"E54.MirrorCS"),sQuery(id+"F11.wireOp",EDGE,"E55.MirrorCS"),sQuery(id+"F11.wireOp",EDGE,"E56.MirrorCS"),sQuery(id+"F11.wireOp",EDGE,"E58.MirrorCS")])]});
            var Q4;
            Q4=makeQuery(id+"F14.opExtrude","SWEPT_BODY",BODY,{"disambiguationData":[OSD([sQuery(id+"F13.wireOp",EDGE,"E62.bottom"),sQuery(id+"F13.wireOp",EDGE,"E62.top"),sQuery(id+"F13.wireOp",EDGE,"E62.left"),sQuery(id+"F13.wireOp",EDGE,"E62.right"),sQuery(id+"F13.wireOp",EDGE,"E63")])]});
            var Q5;
            Q5=makeQuery(id+"F19.opExtrude","SWEPT_BODY",BODY,{"disambiguationData":[OSD([sQuery(id+"F18.wireOp",EDGE,"E78"),sQuery(id+"F18.wireOp",EDGE,"E79"),sQuery(id+"F18.wireOp",EDGE,"E80"),sQuery(id+"F18.wireOp",EDGE,"E81")])]});
            var Q6;
            Q6=makeQuery(id+"F21.opPattern","COPY",BODY,{"derivedFrom":makeQuery(id+"F19.opExtrude","SWEPT_BODY",BODY,{"disambiguationData":[OSD([sQuery(id+"F18.wireOp",EDGE,"E78"),sQuery(id+"F18.wireOp",EDGE,"E79"),sQuery(id+"F18.wireOp",EDGE,"E80"),sQuery(id+"F18.wireOp",EDGE,"E81")])]}),"instanceName":"1"});
            var Q7;
            Q7=makeQuery(id+"F22.opPattern","COPY",BODY,{"derivedFrom":makeQuery(id+"F21.opPattern","COPY",BODY,{"derivedFrom":makeQuery(id+"F19.opExtrude","SWEPT_BODY",BODY,{"disambiguationData":[OSD([sQuery(id+"F18.wireOp",EDGE,"E78"),sQuery(id+"F18.wireOp",EDGE,"E79"),sQuery(id+"F18.wireOp",EDGE,"E80"),sQuery(id+"F18.wireOp",EDGE,"E81")])]}),"instanceName":"1"}),"instanceName":"1"});
            var Q8;
            Q8=makeQuery(id+"F23.opPattern","COPY",BODY,{"derivedFrom":makeQuery(id+"F22.opPattern","COPY",BODY,{"derivedFrom":makeQuery(id+"F21.opPattern","COPY",BODY,{"derivedFrom":makeQuery(id+"F19.opExtrude","SWEPT_BODY",BODY,{"disambiguationData":[OSD([sQuery(id+"F18.wireOp",EDGE,"E78"),sQuery(id+"F18.wireOp",EDGE,"E79"),sQuery(id+"F18.wireOp",EDGE,"E80"),sQuery(id+"F18.wireOp",EDGE,"E81")])]}),"instanceName":"1"}),"instanceName":"1"}),"instanceName":"1"});
            var Q9;
            Q9=makeQuery(id+"F24.opPattern","COPY",BODY,{"derivedFrom":makeQuery(id+"F23.opPattern","COPY",BODY,{"derivedFrom":makeQuery(id+"F22.opPattern","COPY",BODY,{"derivedFrom":makeQuery(id+"F21.opPattern","COPY",BODY,{"derivedFrom":makeQuery(id+"F19.opExtrude","SWEPT_BODY",BODY,{"disambiguationData":[OSD([sQuery(id+"F18.wireOp",EDGE,"E78"),sQuery(id+"F18.wireOp",EDGE,"E79"),sQuery(id+"F18.wireOp",EDGE,"E80"),sQuery(id+"F18.wireOp",EDGE,"E81")])]}),"instanceName":"1"}),"instanceName":"1"}),"instanceName":"1"}),"instanceName":"1"});
            var Q10;
            Q10=makeQuery(id+"F27.opPattern","COPY",BODY,{"derivedFrom":makeQuery(id+"F22.opPattern","COPY",BODY,{"derivedFrom":makeQuery(id+"F21.opPattern","COPY",BODY,{"derivedFrom":makeQuery(id+"F19.opExtrude","SWEPT_BODY",BODY,{"disambiguationData":[OSD([sQuery(id+"F18.wireOp",EDGE,"E78"),sQuery(id+"F18.wireOp",EDGE,"E79"),sQuery(id+"F18.wireOp",EDGE,"E80"),sQuery(id+"F18.wireOp",EDGE,"E81")])]}),"instanceName":"1"}),"instanceName":"1"}),"instanceName":"1"});
            var Q11;
            Q11=makeQuery(id+"F27.opPattern","COPY",BODY,{"derivedFrom":makeQuery(id+"F23.opPattern","COPY",BODY,{"derivedFrom":makeQuery(id+"F22.opPattern","COPY",BODY,{"derivedFrom":makeQuery(id+"F21.opPattern","COPY",BODY,{"derivedFrom":makeQuery(id+"F19.opExtrude","SWEPT_BODY",BODY,{"disambiguationData":[OSD([sQuery(id+"F18.wireOp",EDGE,"E78"),sQuery(id+"F18.wireOp",EDGE,"E79"),sQuery(id+"F18.wireOp",EDGE,"E80"),sQuery(id+"F18.wireOp",EDGE,"E81")])]}),"instanceName":"1"}),"instanceName":"1"}),"instanceName":"1"}),"instanceName":"1"});
            var Q12;
            Q12=qCreatedBy(id+"F25.planeOp",FACE);
            mirror(context, id + "F29", {"entities" : qUnion([Q0, Q1, Q2, Q3, Q4, Q5, Q6, Q7, Q8, Q9, Q10, Q11]), "mirrorPlane" : qUnion([Q12])});
        }
        {
            var Q0;
            Q0=makeQuery(id+"F1.opExtrude","SWEPT_BODY",BODY,{"disambiguationData":[OSD([sQuery(id+"F0.wireOp",EDGE,"E0"),sQuery(id+"F0.wireOp",EDGE,"E1"),sQuery(id+"F0.wireOp",EDGE,"E2"),sQuery(id+"F0.wireOp",EDGE,"E3"),sQuery(id+"F0.wireOp",EDGE,"E4"),sQuery(id+"F0.wireOp",EDGE,"E5"),sQuery(id+"F0.wireOp",EDGE,"E6"),sQuery(id+"F0.wireOp",EDGE,"E7"),sQuery(id+"F0.wireOp",EDGE,"E8"),sQuery(id+"F0.wireOp",EDGE,"E9"),sQuery(id+"F0.wireOp",EDGE,"E10"),sQuery(id+"F0.wireOp",EDGE,"E11"),sQuery(id+"F0.wireOp",EDGE,"E12"),sQuery(id+"F0.wireOp",EDGE,"E13"),sQuery(id+"F0.wireOp",EDGE,"E14"),sQuery(id+"F0.wireOp",EDGE,"E15"),sQuery(id+"F0.wireOp",EDGE,"E20")])]});
            var Q1;
            Q1=makeQuery(id+"F10.opExtrude","SWEPT_BODY",BODY,{"disambiguationData":[OSD([sQuery(id+"F9.wireOp",EDGE,"E39"),sQuery(id+"F9.wireOp",EDGE,"E42"),sQuery(id+"F9.wireOp",EDGE,"E43"),sQuery(id+"F9.wireOp",EDGE,"E44")])]});
            var Q2;
            Q2=makeQuery(id+"F12.opExtrude","SWEPT_BODY",BODY,{"disambiguationData":[OSD([sQuery(id+"F9.wireOp",EDGE,"E43"),sQuery(id+"F9.wireOp",EDGE,"E44"),sQuery(id+"F11.wireOp",EDGE,"E49"),sQuery(id+"F11.wireOp",EDGE,"E50"),sQuery(id+"F11.wireOp",EDGE,"E51"),sQuery(id+"F11.wireOp",EDGE,"E52")])]});
            var Q3;
            Q3=makeQuery(id+"F12.opExtrude","SWEPT_BODY",BODY,{"disambiguationData":[OSD([sQuery(id+"F9.wireOp",EDGE,"E43"),sQuery(id+"F9.wireOp",EDGE,"E44"),sQuery(id+"F11.wireOp",EDGE,"E54.MirrorCS"),sQuery(id+"F11.wireOp",EDGE,"E55.MirrorCS"),sQuery(id+"F11.wireOp",EDGE,"E56.MirrorCS"),sQuery(id+"F11.wireOp",EDGE,"E58.MirrorCS")])]});
            var Q4;
            Q4=makeQuery(id+"F14.opExtrude","SWEPT_BODY",BODY,{"disambiguationData":[OSD([sQuery(id+"F13.wireOp",EDGE,"E62.bottom"),sQuery(id+"F13.wireOp",EDGE,"E62.top"),sQuery(id+"F13.wireOp",EDGE,"E62.left"),sQuery(id+"F13.wireOp",EDGE,"E62.right"),sQuery(id+"F13.wireOp",EDGE,"E63")])]});
            var Q5;
            Q5=makeQuery(id+"F21.opPattern","COPY",BODY,{"derivedFrom":makeQuery(id+"F19.opExtrude","SWEPT_BODY",BODY,{"disambiguationData":[OSD([sQuery(id+"F18.wireOp",EDGE,"E78"),sQuery(id+"F18.wireOp",EDGE,"E79"),sQuery(id+"F18.wireOp",EDGE,"E80"),sQuery(id+"F18.wireOp",EDGE,"E81")])]}),"instanceName":"1"});
            var Q6;
            Q6=makeQuery(id+"F22.opPattern","COPY",BODY,{"derivedFrom":makeQuery(id+"F21.opPattern","COPY",BODY,{"derivedFrom":makeQuery(id+"F19.opExtrude","SWEPT_BODY",BODY,{"disambiguationData":[OSD([sQuery(id+"F18.wireOp",EDGE,"E78"),sQuery(id+"F18.wireOp",EDGE,"E79"),sQuery(id+"F18.wireOp",EDGE,"E80"),sQuery(id+"F18.wireOp",EDGE,"E81")])]}),"instanceName":"1"}),"instanceName":"1"});
            var Q7;
            Q7=makeQuery(id+"F23.opPattern","COPY",BODY,{"derivedFrom":makeQuery(id+"F22.opPattern","COPY",BODY,{"derivedFrom":makeQuery(id+"F21.opPattern","COPY",BODY,{"derivedFrom":makeQuery(id+"F19.opExtrude","SWEPT_BODY",BODY,{"disambiguationData":[OSD([sQuery(id+"F18.wireOp",EDGE,"E78"),sQuery(id+"F18.wireOp",EDGE,"E79"),sQuery(id+"F18.wireOp",EDGE,"E80"),sQuery(id+"F18.wireOp",EDGE,"E81")])]}),"instanceName":"1"}),"instanceName":"1"}),"instanceName":"1"});
            var Q8;
            Q8=makeQuery(id+"F24.opPattern","COPY",BODY,{"derivedFrom":makeQuery(id+"F23.opPattern","COPY",BODY,{"derivedFrom":makeQuery(id+"F22.opPattern","COPY",BODY,{"derivedFrom":makeQuery(id+"F21.opPattern","COPY",BODY,{"derivedFrom":makeQuery(id+"F19.opExtrude","SWEPT_BODY",BODY,{"disambiguationData":[OSD([sQuery(id+"F18.wireOp",EDGE,"E78"),sQuery(id+"F18.wireOp",EDGE,"E79"),sQuery(id+"F18.wireOp",EDGE,"E80"),sQuery(id+"F18.wireOp",EDGE,"E81")])]}),"instanceName":"1"}),"instanceName":"1"}),"instanceName":"1"}),"instanceName":"1"});
            var Q9;
            Q9=makeQuery(id+"F27.opPattern","COPY",BODY,{"derivedFrom":makeQuery(id+"F22.opPattern","COPY",BODY,{"derivedFrom":makeQuery(id+"F21.opPattern","COPY",BODY,{"derivedFrom":makeQuery(id+"F19.opExtrude","SWEPT_BODY",BODY,{"disambiguationData":[OSD([sQuery(id+"F18.wireOp",EDGE,"E78"),sQuery(id+"F18.wireOp",EDGE,"E79"),sQuery(id+"F18.wireOp",EDGE,"E80"),sQuery(id+"F18.wireOp",EDGE,"E81")])]}),"instanceName":"1"}),"instanceName":"1"}),"instanceName":"1"});
            var Q10;
            Q10=makeQuery(id+"F27.opPattern","COPY",BODY,{"derivedFrom":makeQuery(id+"F23.opPattern","COPY",BODY,{"derivedFrom":makeQuery(id+"F22.opPattern","COPY",BODY,{"derivedFrom":makeQuery(id+"F21.opPattern","COPY",BODY,{"derivedFrom":makeQuery(id+"F19.opExtrude","SWEPT_BODY",BODY,{"disambiguationData":[OSD([sQuery(id+"F18.wireOp",EDGE,"E78"),sQuery(id+"F18.wireOp",EDGE,"E79"),sQuery(id+"F18.wireOp",EDGE,"E80"),sQuery(id+"F18.wireOp",EDGE,"E81")])]}),"instanceName":"1"}),"instanceName":"1"}),"instanceName":"1"}),"instanceName":"1"});
            var Q11;
            Q11=makeQuery(id+"F29.opPattern","COPY",BODY,{"derivedFrom":makeQuery(id+"F1.opExtrude","SWEPT_BODY",BODY,{"disambiguationData":[OSD([sQuery(id+"F0.wireOp",EDGE,"E0"),sQuery(id+"F0.wireOp",EDGE,"E1"),sQuery(id+"F0.wireOp",EDGE,"E2"),sQuery(id+"F0.wireOp",EDGE,"E3"),sQuery(id+"F0.wireOp",EDGE,"E4"),sQuery(id+"F0.wireOp",EDGE,"E5"),sQuery(id+"F0.wireOp",EDGE,"E6"),sQuery(id+"F0.wireOp",EDGE,"E7"),sQuery(id+"F0.wireOp",EDGE,"E8"),sQuery(id+"F0.wireOp",EDGE,"E9"),sQuery(id+"F0.wireOp",EDGE,"E10"),sQuery(id+"F0.wireOp",EDGE,"E11"),sQuery(id+"F0.wireOp",EDGE,"E12"),sQuery(id+"F0.wireOp",EDGE,"E13"),sQuery(id+"F0.wireOp",EDGE,"E14"),sQuery(id+"F0.wireOp",EDGE,"E15"),sQuery(id+"F0.wireOp",EDGE,"E20")])]}),"instanceName":"1"});
            var Q12;
            Q12=makeQuery(id+"F29.opPattern","COPY",BODY,{"derivedFrom":makeQuery(id+"F10.opExtrude","SWEPT_BODY",BODY,{"disambiguationData":[OSD([sQuery(id+"F9.wireOp",EDGE,"E39"),sQuery(id+"F9.wireOp",EDGE,"E42"),sQuery(id+"F9.wireOp",EDGE,"E43"),sQuery(id+"F9.wireOp",EDGE,"E44")])]}),"instanceName":"1"});
            var Q13;
            Q13=makeQuery(id+"F29.opPattern","COPY",BODY,{"derivedFrom":makeQuery(id+"F12.opExtrude","SWEPT_BODY",BODY,{"disambiguationData":[OSD([sQuery(id+"F9.wireOp",EDGE,"E43"),sQuery(id+"F9.wireOp",EDGE,"E44"),sQuery(id+"F11.wireOp",EDGE,"E49"),sQuery(id+"F11.wireOp",EDGE,"E50"),sQuery(id+"F11.wireOp",EDGE,"E51"),sQuery(id+"F11.wireOp",EDGE,"E52")])]}),"instanceName":"1"});
            var Q14;
            Q14=makeQuery(id+"F29.opPattern","COPY",BODY,{"derivedFrom":makeQuery(id+"F12.opExtrude","SWEPT_BODY",BODY,{"disambiguationData":[OSD([sQuery(id+"F9.wireOp",EDGE,"E43"),sQuery(id+"F9.wireOp",EDGE,"E44"),sQuery(id+"F11.wireOp",EDGE,"E54.MirrorCS"),sQuery(id+"F11.wireOp",EDGE,"E55.MirrorCS"),sQuery(id+"F11.wireOp",EDGE,"E56.MirrorCS"),sQuery(id+"F11.wireOp",EDGE,"E58.MirrorCS")])]}),"instanceName":"1"});
            var Q15;
            Q15=makeQuery(id+"F29.opPattern","COPY",BODY,{"derivedFrom":makeQuery(id+"F14.opExtrude","SWEPT_BODY",BODY,{"disambiguationData":[OSD([sQuery(id+"F13.wireOp",EDGE,"E62.bottom"),sQuery(id+"F13.wireOp",EDGE,"E62.top"),sQuery(id+"F13.wireOp",EDGE,"E62.left"),sQuery(id+"F13.wireOp",EDGE,"E62.right"),sQuery(id+"F13.wireOp",EDGE,"E63")])]}),"instanceName":"1"});
            var Q16;
            Q16=makeQuery(id+"F29.opPattern","COPY",BODY,{"derivedFrom":makeQuery(id+"F21.opPattern","COPY",BODY,{"derivedFrom":makeQuery(id+"F19.opExtrude","SWEPT_BODY",BODY,{"disambiguationData":[OSD([sQuery(id+"F18.wireOp",EDGE,"E78"),sQuery(id+"F18.wireOp",EDGE,"E79"),sQuery(id+"F18.wireOp",EDGE,"E80"),sQuery(id+"F18.wireOp",EDGE,"E81")])]}),"instanceName":"1"}),"instanceName":"1"});
            var Q17;
            Q17=makeQuery(id+"F29.opPattern","COPY",BODY,{"derivedFrom":makeQuery(id+"F22.opPattern","COPY",BODY,{"derivedFrom":makeQuery(id+"F21.opPattern","COPY",BODY,{"derivedFrom":makeQuery(id+"F19.opExtrude","SWEPT_BODY",BODY,{"disambiguationData":[OSD([sQuery(id+"F18.wireOp",EDGE,"E78"),sQuery(id+"F18.wireOp",EDGE,"E79"),sQuery(id+"F18.wireOp",EDGE,"E80"),sQuery(id+"F18.wireOp",EDGE,"E81")])]}),"instanceName":"1"}),"instanceName":"1"}),"instanceName":"1"});
            var Q18;
            Q18=makeQuery(id+"F29.opPattern","COPY",BODY,{"derivedFrom":makeQuery(id+"F23.opPattern","COPY",BODY,{"derivedFrom":makeQuery(id+"F22.opPattern","COPY",BODY,{"derivedFrom":makeQuery(id+"F21.opPattern","COPY",BODY,{"derivedFrom":makeQuery(id+"F19.opExtrude","SWEPT_BODY",BODY,{"disambiguationData":[OSD([sQuery(id+"F18.wireOp",EDGE,"E78"),sQuery(id+"F18.wireOp",EDGE,"E79"),sQuery(id+"F18.wireOp",EDGE,"E80"),sQuery(id+"F18.wireOp",EDGE,"E81")])]}),"instanceName":"1"}),"instanceName":"1"}),"instanceName":"1"}),"instanceName":"1"});
            var Q19;
            Q19=makeQuery(id+"F29.opPattern","COPY",BODY,{"derivedFrom":makeQuery(id+"F24.opPattern","COPY",BODY,{"derivedFrom":makeQuery(id+"F23.opPattern","COPY",BODY,{"derivedFrom":makeQuery(id+"F22.opPattern","COPY",BODY,{"derivedFrom":makeQuery(id+"F21.opPattern","COPY",BODY,{"derivedFrom":makeQuery(id+"F19.opExtrude","SWEPT_BODY",BODY,{"disambiguationData":[OSD([sQuery(id+"F18.wireOp",EDGE,"E78"),sQuery(id+"F18.wireOp",EDGE,"E79"),sQuery(id+"F18.wireOp",EDGE,"E80"),sQuery(id+"F18.wireOp",EDGE,"E81")])]}),"instanceName":"1"}),"instanceName":"1"}),"instanceName":"1"}),"instanceName":"1"}),"instanceName":"1"});
            var Q20;
            Q20=makeQuery(id+"F29.opPattern","COPY",BODY,{"derivedFrom":makeQuery(id+"F27.opPattern","COPY",BODY,{"derivedFrom":makeQuery(id+"F22.opPattern","COPY",BODY,{"derivedFrom":makeQuery(id+"F21.opPattern","COPY",BODY,{"derivedFrom":makeQuery(id+"F19.opExtrude","SWEPT_BODY",BODY,{"disambiguationData":[OSD([sQuery(id+"F18.wireOp",EDGE,"E78"),sQuery(id+"F18.wireOp",EDGE,"E79"),sQuery(id+"F18.wireOp",EDGE,"E80"),sQuery(id+"F18.wireOp",EDGE,"E81")])]}),"instanceName":"1"}),"instanceName":"1"}),"instanceName":"1"}),"instanceName":"1"});
            var Q21;
            Q21=makeQuery(id+"F29.opPattern","COPY",BODY,{"derivedFrom":makeQuery(id+"F27.opPattern","COPY",BODY,{"derivedFrom":makeQuery(id+"F23.opPattern","COPY",BODY,{"derivedFrom":makeQuery(id+"F22.opPattern","COPY",BODY,{"derivedFrom":makeQuery(id+"F21.opPattern","COPY",BODY,{"derivedFrom":makeQuery(id+"F19.opExtrude","SWEPT_BODY",BODY,{"disambiguationData":[OSD([sQuery(id+"F18.wireOp",EDGE,"E78"),sQuery(id+"F18.wireOp",EDGE,"E79"),sQuery(id+"F18.wireOp",EDGE,"E80"),sQuery(id+"F18.wireOp",EDGE,"E81")])]}),"instanceName":"1"}),"instanceName":"1"}),"instanceName":"1"}),"instanceName":"1"}),"instanceName":"1"});
            booleanBodies(context, id + "F30", {"operationType" : BooleanOperationType.UNION, "tools" : qUnion([Q0, Q1, Q2, Q3, Q4, Q5, Q6, Q7, Q8, Q9, Q10, Q11, Q12, Q13, Q14, Q15, Q16, Q17, Q18, Q19, Q20, Q21])});
        }
    });
